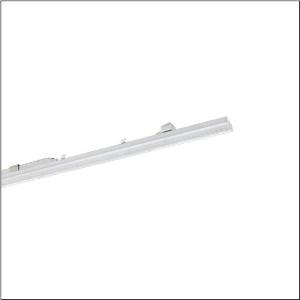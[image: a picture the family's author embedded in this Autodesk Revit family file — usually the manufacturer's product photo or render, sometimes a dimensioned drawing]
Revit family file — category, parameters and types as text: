
# Revit family: tl_l_5wd7a8p0b2c5
name_source: partatom
category: Lighting Fixtures
units: mm (PartAtom-declared; Revit-internal decimal feet)

## family parameters
Cut with Voids When Loaded = No
Host = Face
Light Source = No
Part Type = Normal
Room Calculation Point = No
Round Connector Dimension = Use Diameter
Shared = No

## types (1)
- --- (1 x LED, 9800 lm, 63.4 W, 4000K)
    Apparent Load = 63 VA
    CIE Flux Codes = 49 84 98 100 100
    Color Rendering = 80
    Color Temperature = 4000K
    Default Elevation = 1800 mm
    Description = TL L, luminaire insert, of sheet steel, galvanised, coil coated, white, length: 1.500mm, width: 66mm, height: 67mm, micro fuse,LED light colour: 840, control gear: DALI, with terminal, 5-pole, mains connection: 230..240V, AC, 50/60Hz, rated input power: 30W, primary optical cover: cover, of PMMA, light emission: direct distribution, protection rating (complete): as luminaire, insulation class (complete): insulation class I (protective earthing), certification: CE, impact resistance: IK06, permissible ambient temperature for indoor applications: -35..+35°C, standard: NMF01, packaging unit: 1 piece
    Height = 120 mm
    Lamp = 1 x LED
    Lamp Light Flux = 9800 lm
    Lamp Power = 63.4 W
    Lamp count = 1
    Length = 1690 mm
    Luminous efficacy = 155 lm/W
    Manufacturer = Siteco
    ModVariant = No
    Model = 5WD7A8P0B2C5
    Mounting Place = Ceiling
    Mounting Type = Pendant
    Number of Poles = 1
    OnlyDefault = Yes
    Power Factor = 1
    Product Name = TL L
    Product group = luminaire insert
    ProductGroupID = 901
    Protection Class = Protection class I
    Protection Degree = Degree of protection
    RLX_Detail_Level = 1
    RLX_Emergency_Light_Flux = 0 lm
    RLX_Emergency_Type = 0
    RLX_Emergency_Type_DB = No
    RlxData = <blob elided: 17273 chars, md5=3141ae18>
    Socket = socket
    Standby Power = 0 W
    System Light Flux = 9800 lm
    System Power = 63 W
    Type Comments = factory setting: luminous flux: 100 % | dim-lin: 254 | 420 mA
    Type Image = l_1294382.jpg
    URL = http://relux.com
    VarID = @adj_000581
    Voltage = 0 V
    Weight = 0.00 kg
    Width = 208 mm

## geometry (parser evidence)
native form markers: Blend x4, Sweep x11
no freeform markers — native parametric forms only
